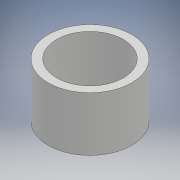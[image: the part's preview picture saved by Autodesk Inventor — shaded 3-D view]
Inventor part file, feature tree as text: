
AUTODESK INVENTOR PART (.ipt)
format: ipt  version: 2018.2 (Build 222227000, 227)  size: 94,720 bytes
history: native  units: mm
features: other x1, extrude x1, sketch x1
ambient origin geometry x8: Origin, YZ Plane, XZ Plane, XY Plane, X Axis, Y Axis, Z Axis, Center Point
bodies: Body1 (feature_tree)
feature tree (3):
  other  "ソリッド1"
  extrude  "押し出し1"  Depth=6.5mm TaperAngle=0.0deg
  sketch  "スケッチ1"
